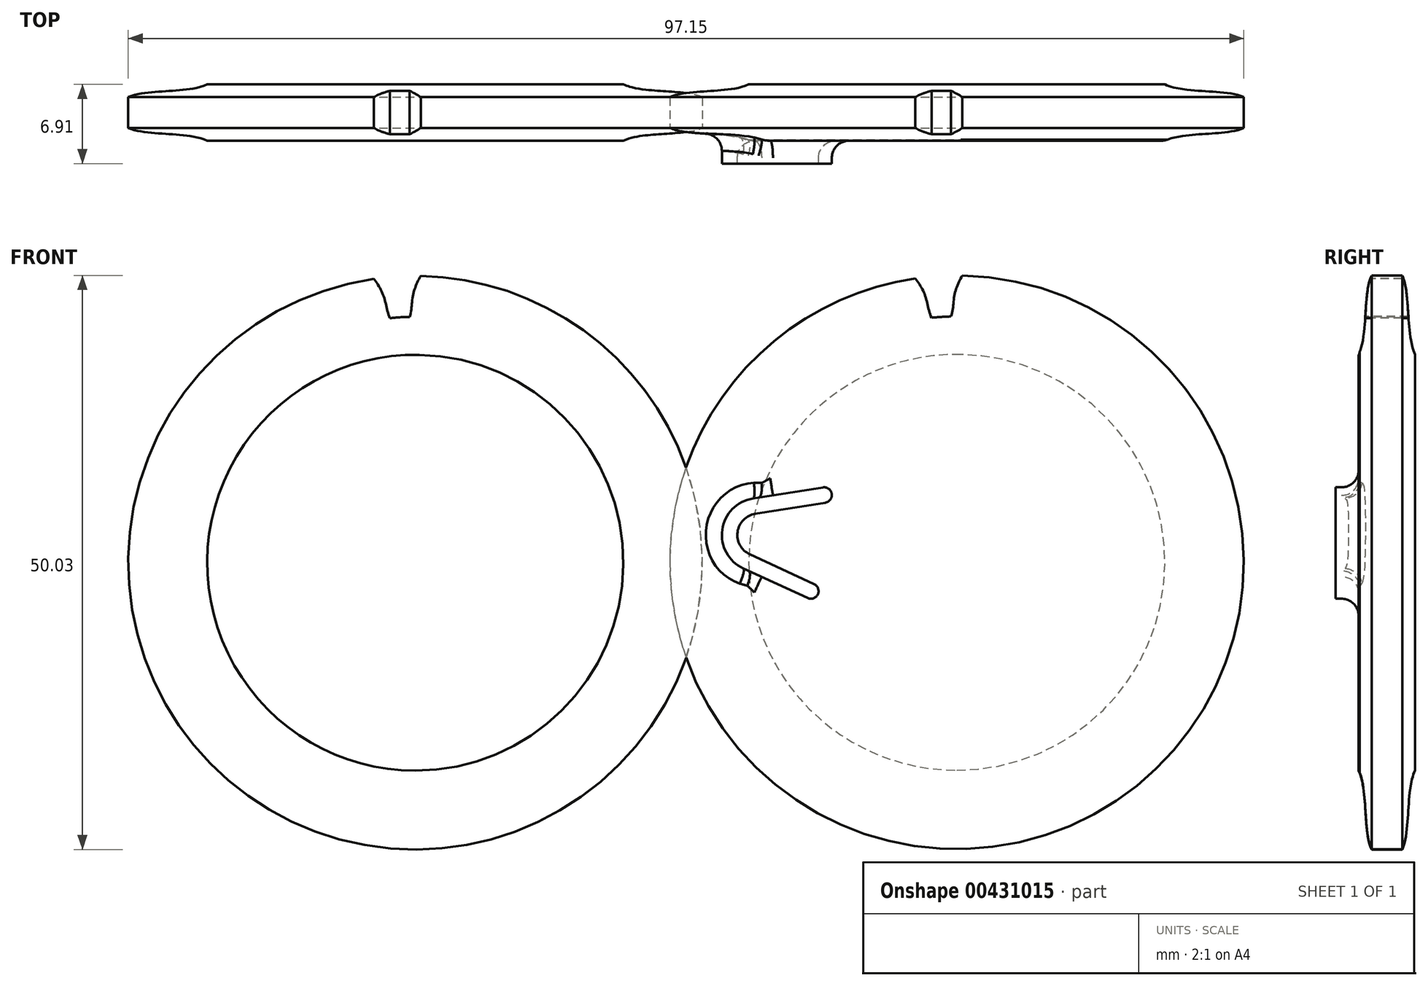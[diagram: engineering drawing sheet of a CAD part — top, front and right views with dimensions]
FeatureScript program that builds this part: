
annotation { "Feature Type Name" : "Feature", "Feature Type Description" : "" }
export const myFeature = defineFeature(function(context is Context, id is Id, definition is map)
    precondition{}
    {
        {
            var Q0;
            Q0=qCreatedBy(makeId("Front.planeOp"),FACE);
            var sketch = newSketch(context, id + "F0", { "sketchPlane" : qUnion([Q0])});
            skCircle(sketch, "E0", {"center": v(0, 0) * mm, "radius": 5.22 * mm});
            skPoint(sketch, "E0.first.point", {"position": v(-0.14, 5.22) * mm});
            skPoint(sketch, "E0.second.point", {"position": v(0.18, -5.22) * mm});
            skPoint(sketch, "E0.third.point", {"position": v(5.22, 0.15) * mm});
            skSolve(sketch);
        }
        {
            var Q0;
            Q0=qCreatedBy(makeId("Front.planeOp"),FACE);
            var sketch = newSketch(context, id + "F1", { "sketchPlane" : qUnion([Q0])});
            skCircle(sketch, "E1.0", {"center": v(0, 0) * mm, "radius": 5.22 * mm});
            skLineSegment(sketch, "E2", {"start": v(0, 125) * mm, "end": v(0, -125) * mm, "construction": true});
            skLineSegment(sketch, "E3", {"start": v(-125, 0) * mm, "end": v(125, 0) * mm, "construction": true});
            skArc(sketch, "E4", {"start": v(-3.61, 24.74) * mm, "mid": v(1.57, -24.95) * mm, "end": v(0.48, 25) * mm, "construction": true});
            skCircle(sketch, "E5", {"center": v(0, 0) * mm, "radius": 23.24 * mm, "construction": true});
            skCircle(sketch, "E6", {"center": v(0, 0) * mm, "radius": 21.43 * mm, "construction": true});
            skLineSegment(sketch, "E7", {"start": v(0, 0) * mm, "end": v(-4.4, 25.96) * mm, "construction": true});
            skLineSegment(sketch, "E8", {"start": v(0, 0) * mm, "end": v(1.13, 26.88) * mm, "construction": true});
            skFitSpline(sketch, "E9", {"points": [v(-3.61, 24.74) * mm, v(-2.7, 23.08) * mm, v(-2.2, 21.32) * mm, v(-1.5, 20.62) * mm], "startDerivative": vector(3.33, -4.08) * mm, "endDerivative": vector(3.08, -2.02) * mm});
            skFitSpline(sketch, "E10.MirrorCS", {"points": [v(0.48, 25) * mm, v(-0.2, 23.23) * mm, v(-0.5, 21.43) * mm, v(-1.1, 20.65) * mm], "startDerivative": vector(-2.8, -4.47) * mm, "endDerivative": vector(-2.8, -2.4) * mm});
            skArc(sketch, "E11", {"start": v(-2.2, 21.32) * mm, "mid": v(-1.35, 21.39) * mm, "end": v(-0.5, 21.43) * mm});
            skArc(sketch, "E12", {"start": v(-4.17, 24.65) * mm, "mid": v(-3.9, 24.7) * mm, "end": v(-3.61, 24.74) * mm});
            skArc(sketch, "E13.trimOffspring", {"start": v(0.48, 25) * mm, "mid": v(0.77, 24.99) * mm, "end": v(1.05, 24.98) * mm});
            skArc(sketch, "E14.1.0", {"start": v(-4.72, 24.55) * mm, "mid": v(-4.45, 24.6) * mm, "end": v(-4.17, 24.65) * mm});
            skArc(sketch, "E14.1.1", {"start": v(-9.2, 23.24) * mm, "mid": v(-8.94, 23.35) * mm, "end": v(-8.68, 23.45) * mm});
            skArc(sketch, "E14.1.2", {"start": v(-6.58, 20.4) * mm, "mid": v(-5.76, 20.64) * mm, "end": v(-4.94, 20.86) * mm});
            skArc(sketch, "E14.2.0", {"start": v(-9.72, 23.03) * mm, "mid": v(-9.46, 23.14) * mm, "end": v(-9.2, 23.24) * mm});
            skArc(sketch, "E14.2.1", {"start": v(-13.84, 20.82) * mm, "mid": v(-13.6, 20.98) * mm, "end": v(-13.36, 21.13) * mm});
            skArc(sketch, "E14.2.2", {"start": v(-10.68, 18.58) * mm, "mid": v(-9.93, 19) * mm, "end": v(-9.16, 19.37) * mm});
            skArc(sketch, "E14.3.0", {"start": v(-14.3, 20.5) * mm, "mid": v(-14.07, 20.67) * mm, "end": v(-13.84, 20.82) * mm});
            skArc(sketch, "E14.3.1", {"start": v(-17.86, 17.5) * mm, "mid": v(-17.66, 17.7) * mm, "end": v(-17.46, 17.89) * mm});
            skArc(sketch, "E14.3.2", {"start": v(-14.3, 15.96) * mm, "mid": v(-13.66, 16.51) * mm, "end": v(-13, 17.04) * mm});
            skArc(sketch, "E14.4.0", {"start": v(-18.25, 17.08) * mm, "mid": v(-18.06, 17.29) * mm, "end": v(-17.86, 17.5) * mm});
            skArc(sketch, "E14.4.1", {"start": v(-21.1, 13.4) * mm, "mid": v(-20.96, 13.63) * mm, "end": v(-20.8, 13.87) * mm});
            skArc(sketch, "E14.4.2", {"start": v(-17.31, 12.63) * mm, "mid": v(-16.8, 13.31) * mm, "end": v(-16.25, 13.97) * mm});
            skArc(sketch, "E14.5.0", {"start": v(-21.4, 12.92) * mm, "mid": v(-21.26, 13.16) * mm, "end": v(-21.1, 13.4) * mm});
            skArc(sketch, "E14.5.1", {"start": v(-23.43, 8.71) * mm, "mid": v(-23.33, 8.98) * mm, "end": v(-23.23, 9.24) * mm});
            skArc(sketch, "E14.5.2", {"start": v(-19.56, 8.76) * mm, "mid": v(-19.2, 9.53) * mm, "end": v(-18.8, 10.29) * mm});
            skArc(sketch, "E14.6.0", {"start": v(-23.62, 8.18) * mm, "mid": v(-23.53, 8.45) * mm, "end": v(-23.43, 8.71) * mm});
            skArc(sketch, "E14.6.1", {"start": v(-24.73, 3.65) * mm, "mid": v(-24.69, 3.93) * mm, "end": v(-24.64, 4.2) * mm});
            skArc(sketch, "E14.6.2", {"start": v(-20.95, 4.5) * mm, "mid": v(-20.76, 5.33) * mm, "end": v(-20.53, 6.15) * mm});
            skArc(sketch, "E14.7.0", {"start": v(-24.8, 3.1) * mm, "mid": v(-24.77, 3.37) * mm, "end": v(-24.73, 3.65) * mm});
            skArc(sketch, "E14.7.1", {"start": v(-24.95, -1.57) * mm, "mid": v(-24.97, -1.29) * mm, "end": v(-24.98, -1) * mm});
            skArc(sketch, "E14.7.2", {"start": v(-21.43, 0.04) * mm, "mid": v(-21.41, 0.9) * mm, "end": v(-21.36, 1.75) * mm});
            skArc(sketch, "E14.8.0", {"start": v(-24.9, -2.13) * mm, "mid": v(-24.93, -1.85) * mm, "end": v(-24.95, -1.57) * mm});
            skArc(sketch, "E14.8.1", {"start": v(-24.08, -6.72) * mm, "mid": v(-24.15, -6.45) * mm, "end": v(-24.22, -6.18) * mm});
            skArc(sketch, "E14.8.2", {"start": v(-20.97, -4.41) * mm, "mid": v(-21.13, -3.57) * mm, "end": v(-21.26, -2.73) * mm});
            skArc(sketch, "E14.9.0", {"start": v(-23.92, -7.26) * mm, "mid": v(-24, -7) * mm, "end": v(-24.08, -6.72) * mm});
            skArc(sketch, "E14.9.1", {"start": v(-22.15, -11.58) * mm, "mid": v(-22.28, -11.33) * mm, "end": v(-22.4, -11.08) * mm});
            skArc(sketch, "E14.9.2", {"start": v(-19.6, -8.68) * mm, "mid": v(-19.93, -7.9) * mm, "end": v(-20.23, -7.09) * mm});
            skArc(sketch, "E14.10.0", {"start": v(-21.89, -12.08) * mm, "mid": v(-22.02, -11.83) * mm, "end": v(-22.15, -11.58) * mm});
            skArc(sketch, "E14.10.1", {"start": v(-19.26, -15.94) * mm, "mid": v(-19.44, -15.72) * mm, "end": v(-19.62, -15.5) * mm});
            skArc(sketch, "E14.10.2", {"start": v(-17.36, -12.56) * mm, "mid": v(-17.85, -11.86) * mm, "end": v(-18.3, -11.14) * mm});
            skArc(sketch, "E14.11.0", {"start": v(-18.9, -16.37) * mm, "mid": v(-19.08, -16.15) * mm, "end": v(-19.26, -15.94) * mm});
            skArc(sketch, "E14.11.1", {"start": v(-15.53, -19.6) * mm, "mid": v(-15.75, -19.42) * mm, "end": v(-15.97, -19.24) * mm});
            skArc(sketch, "E14.11.2", {"start": v(-14.37, -15.9) * mm, "mid": v(-15, -15.31) * mm, "end": v(-15.6, -14.7) * mm});
            skArc(sketch, "E14.12.0", {"start": v(-15.08, -19.94) * mm, "mid": v(-15.3, -19.77) * mm, "end": v(-15.53, -19.6) * mm});
            skArc(sketch, "E14.12.1", {"start": v(-11.12, -22.4) * mm, "mid": v(-11.37, -22.27) * mm, "end": v(-11.62, -22.14) * mm});
            skArc(sketch, "E14.12.2", {"start": v(-10.75, -18.54) * mm, "mid": v(-11.48, -18.1) * mm, "end": v(-12.2, -17.62) * mm});
            skArc(sketch, "E14.13.0", {"start": v(-10.6, -22.64) * mm, "mid": v(-10.86, -22.52) * mm, "end": v(-11.12, -22.4) * mm});
            skArc(sketch, "E14.13.1", {"start": v(-6.22, -24.21) * mm, "mid": v(-6.49, -24.14) * mm, "end": v(-6.76, -24.07) * mm});
            skArc(sketch, "E14.13.2", {"start": v(-6.66, -20.37) * mm, "mid": v(-7.47, -20.09) * mm, "end": v(-8.26, -19.77) * mm});
            skArc(sketch, "E14.14.0", {"start": v(-5.67, -24.35) * mm, "mid": v(-5.94, -24.28) * mm, "end": v(-6.22, -24.21) * mm});
            skArc(sketch, "E14.14.1", {"start": v(-1.05, -24.98) * mm, "mid": v(-1.33, -24.96) * mm, "end": v(-1.6, -24.95) * mm});
            skArc(sketch, "E14.14.2", {"start": v(-2.28, -21.3) * mm, "mid": v(-3.13, -21.2) * mm, "end": v(-3.97, -21.06) * mm});
            skArc(sketch, "E14.15.0", {"start": v(-0.48, -25) * mm, "mid": v(-0.77, -24.99) * mm, "end": v(-1.05, -24.98) * mm});
            skArc(sketch, "E14.15.1", {"start": v(4.17, -24.65) * mm, "mid": v(3.9, -24.7) * mm, "end": v(3.61, -24.74) * mm});
            skArc(sketch, "E14.15.2", {"start": v(2.2, -21.32) * mm, "mid": v(1.35, -21.39) * mm, "end": v(0.5, -21.43) * mm});
            skArc(sketch, "E14.16.0", {"start": v(4.72, -24.55) * mm, "mid": v(4.45, -24.6) * mm, "end": v(4.17, -24.65) * mm});
            skArc(sketch, "E14.16.1", {"start": v(9.2, -23.24) * mm, "mid": v(8.94, -23.35) * mm, "end": v(8.68, -23.45) * mm});
            skArc(sketch, "E14.16.2", {"start": v(6.58, -20.4) * mm, "mid": v(5.76, -20.64) * mm, "end": v(4.94, -20.86) * mm});
            skArc(sketch, "E14.17.0", {"start": v(9.72, -23.03) * mm, "mid": v(9.46, -23.14) * mm, "end": v(9.2, -23.24) * mm});
            skArc(sketch, "E14.17.1", {"start": v(13.84, -20.82) * mm, "mid": v(13.6, -20.98) * mm, "end": v(13.36, -21.13) * mm});
            skArc(sketch, "E14.17.2", {"start": v(10.68, -18.58) * mm, "mid": v(9.93, -19) * mm, "end": v(9.16, -19.37) * mm});
            skArc(sketch, "E14.18.0", {"start": v(14.3, -20.5) * mm, "mid": v(14.07, -20.67) * mm, "end": v(13.84, -20.82) * mm});
            skArc(sketch, "E14.18.1", {"start": v(17.86, -17.5) * mm, "mid": v(17.66, -17.7) * mm, "end": v(17.46, -17.89) * mm});
            skArc(sketch, "E14.18.2", {"start": v(14.3, -15.96) * mm, "mid": v(13.66, -16.51) * mm, "end": v(13, -17.04) * mm});
            skArc(sketch, "E14.19.0", {"start": v(18.25, -17.08) * mm, "mid": v(18.06, -17.29) * mm, "end": v(17.86, -17.5) * mm});
            skArc(sketch, "E14.19.1", {"start": v(21.1, -13.4) * mm, "mid": v(20.96, -13.63) * mm, "end": v(20.8, -13.87) * mm});
            skArc(sketch, "E14.19.2", {"start": v(17.31, -12.63) * mm, "mid": v(16.8, -13.31) * mm, "end": v(16.25, -13.97) * mm});
            skArc(sketch, "E14.20.0", {"start": v(21.4, -12.92) * mm, "mid": v(21.26, -13.16) * mm, "end": v(21.1, -13.4) * mm});
            skArc(sketch, "E14.20.1", {"start": v(23.43, -8.71) * mm, "mid": v(23.33, -8.98) * mm, "end": v(23.23, -9.24) * mm});
            skArc(sketch, "E14.20.2", {"start": v(19.56, -8.76) * mm, "mid": v(19.2, -9.53) * mm, "end": v(18.8, -10.29) * mm});
            skArc(sketch, "E14.21.0", {"start": v(23.62, -8.18) * mm, "mid": v(23.53, -8.45) * mm, "end": v(23.43, -8.71) * mm});
            skArc(sketch, "E14.21.1", {"start": v(24.73, -3.65) * mm, "mid": v(24.69, -3.93) * mm, "end": v(24.64, -4.2) * mm});
            skArc(sketch, "E14.21.2", {"start": v(20.95, -4.5) * mm, "mid": v(20.76, -5.33) * mm, "end": v(20.53, -6.15) * mm});
            skArc(sketch, "E14.22.0", {"start": v(24.8, -3.1) * mm, "mid": v(24.77, -3.37) * mm, "end": v(24.73, -3.65) * mm});
            skArc(sketch, "E14.22.1", {"start": v(24.95, 1.57) * mm, "mid": v(24.97, 1.29) * mm, "end": v(24.98, 1) * mm});
            skArc(sketch, "E14.22.2", {"start": v(21.43, -0.04) * mm, "mid": v(21.41, -0.9) * mm, "end": v(21.36, -1.75) * mm});
            skArc(sketch, "E14.23.0", {"start": v(24.9, 2.13) * mm, "mid": v(24.93, 1.85) * mm, "end": v(24.95, 1.57) * mm});
            skArc(sketch, "E14.23.1", {"start": v(24.08, 6.72) * mm, "mid": v(24.15, 6.45) * mm, "end": v(24.22, 6.18) * mm});
            skArc(sketch, "E14.23.2", {"start": v(20.97, 4.41) * mm, "mid": v(21.13, 3.57) * mm, "end": v(21.26, 2.73) * mm});
            skArc(sketch, "E14.24.0", {"start": v(23.92, 7.26) * mm, "mid": v(24, 7) * mm, "end": v(24.08, 6.72) * mm});
            skArc(sketch, "E14.24.1", {"start": v(22.15, 11.58) * mm, "mid": v(22.28, 11.33) * mm, "end": v(22.4, 11.08) * mm});
            skArc(sketch, "E14.24.2", {"start": v(19.6, 8.68) * mm, "mid": v(19.93, 7.9) * mm, "end": v(20.23, 7.09) * mm});
            skArc(sketch, "E14.25.0", {"start": v(21.89, 12.08) * mm, "mid": v(22.02, 11.83) * mm, "end": v(22.15, 11.58) * mm});
            skArc(sketch, "E14.25.1", {"start": v(19.26, 15.94) * mm, "mid": v(19.44, 15.72) * mm, "end": v(19.62, 15.5) * mm});
            skArc(sketch, "E14.25.2", {"start": v(17.36, 12.56) * mm, "mid": v(17.85, 11.86) * mm, "end": v(18.3, 11.14) * mm});
            skArc(sketch, "E14.26.0", {"start": v(18.9, 16.37) * mm, "mid": v(19.08, 16.15) * mm, "end": v(19.26, 15.94) * mm});
            skArc(sketch, "E14.26.1", {"start": v(15.53, 19.6) * mm, "mid": v(15.75, 19.42) * mm, "end": v(15.97, 19.24) * mm});
            skArc(sketch, "E14.26.2", {"start": v(14.37, 15.9) * mm, "mid": v(15, 15.31) * mm, "end": v(15.6, 14.7) * mm});
            skArc(sketch, "E14.27.0", {"start": v(15.08, 19.94) * mm, "mid": v(15.3, 19.77) * mm, "end": v(15.53, 19.6) * mm});
            skArc(sketch, "E14.27.1", {"start": v(11.12, 22.4) * mm, "mid": v(11.37, 22.27) * mm, "end": v(11.62, 22.14) * mm});
            skArc(sketch, "E14.27.2", {"start": v(10.75, 18.54) * mm, "mid": v(11.48, 18.1) * mm, "end": v(12.2, 17.62) * mm});
            skArc(sketch, "E14.28.0", {"start": v(10.6, 22.64) * mm, "mid": v(10.86, 22.52) * mm, "end": v(11.12, 22.4) * mm});
            skArc(sketch, "E14.28.1", {"start": v(6.22, 24.21) * mm, "mid": v(6.49, 24.14) * mm, "end": v(6.76, 24.07) * mm});
            skArc(sketch, "E14.28.2", {"start": v(6.66, 20.37) * mm, "mid": v(7.47, 20.09) * mm, "end": v(8.26, 19.77) * mm});
            skArc(sketch, "E14.29.0", {"start": v(5.67, 24.35) * mm, "mid": v(5.94, 24.28) * mm, "end": v(6.22, 24.21) * mm});
            skArc(sketch, "E14.29.1", {"start": v(1.05, 24.98) * mm, "mid": v(1.33, 24.96) * mm, "end": v(1.6, 24.95) * mm});
            skArc(sketch, "E14.29.2", {"start": v(2.28, 21.3) * mm, "mid": v(3.13, 21.2) * mm, "end": v(3.97, 21.06) * mm});
            skArc(sketch, "E15", {"start": v(-3.61, 24.74) * mm, "mid": v(-1.57, 24.95) * mm, "end": v(0.48, 25) * mm});
            skCircle(sketch, "E16", {"center": v(-47.16, -0.04) * mm, "radius": 21.4 * mm});
            skPoint(sketch, "E16.first.point", {"position": v(-56.55, 19.18) * mm});
            skPoint(sketch, "E16.second.point", {"position": v(-28.26, -10.06) * mm});
            skPoint(sketch, "E16.third.point", {"position": v(-59.13, -17.76) * mm});
            skSolve(sketch);
        }
        {
            var Q0;
            Q0=qCreatedBy(makeId("Right.planeOp"),FACE);
            var sketch = newSketch(context, id + "F2", { "sketchPlane" : qUnion([Q0])});
            skPoint(sketch, "E17.0", {"position": v(0, 26.88) * mm});
            skLineSegment(sketch, "E18.bottom", {"start": v(4.9, 0) * mm, "end": v(0, 0) * mm});
            skLineSegment(sketch, "E18.top", {"start": v(3.79, 25) * mm, "end": v(1.12, 25) * mm});
            skLineSegment(sketch, "E18.left", {"start": v(0, 5.22) * mm, "end": v(0, 9.34) * mm});
            skPoint(sketch, "E19.0", {"position": v(0, 5.22) * mm});
            skLineSegment(sketch, "E20.bottom", {"start": v(0, 0) * mm, "end": v(4.9, 0) * mm});
            skLineSegment(sketch, "E21", {"start": v(2.45, 26.88) * mm, "end": v(2.45, -4.73) * mm, "construction": true});
            skFitSpline(sketch, "E22", {"points": [v(1.12, 25) * mm, v(0, 18.12) * mm], "startDerivative": vector(-2.23, -4.75) * mm, "endDerivative": vector(-2.47, -5.27) * mm});
            skLineSegment(sketch, "E23.right", {"start": v(0, 18.12) * mm, "end": v(0, 9.34) * mm});
            skFitSpline(sketch, "E24.MirrorCS", {"points": [v(3.79, 25) * mm, v(4.9, 18.12) * mm], "startDerivative": vector(2.23, -4.75) * mm, "endDerivative": vector(2.47, -5.27) * mm});
            skLineSegment(sketch, "E25.MirrorCS", {"start": v(4.9, 18.12) * mm, "end": v(4.9, 18.12) * mm});
            skLineSegment(sketch, "E26.MirrorCS", {"start": v(4.9, 18.12) * mm, "end": v(4.9, 9.34) * mm});
            skLineSegment(sketch, "E27.MirrorCS", {"start": v(4.9, 9.34) * mm, "end": v(4.9, 9.71) * mm});
            skPoint(sketch, "E28.orphan", {"position": v(4.9, 26.88) * mm});
            skPoint(sketch, "E29.visualSharp", {"position": v(0, 9.34) * mm});
            skPoint(sketch, "E30.visualSharp", {"position": v(4.9, 9.34) * mm});
            skLineSegment(sketch, "E30.filletArc", {"start": v(4.9, 9.71) * mm, "end": v(4.9, 9.71) * mm});
            skPoint(sketch, "E31.0", {"position": v(0, 25.96) * mm});
            skLineSegment(sketch, "E32", {"start": v(0, 25) * mm, "end": v(13.28, 25) * mm, "construction": true});
            skLineSegment(sketch, "E33.0", {"start": v(0, -25) * mm, "end": v(0, 0) * mm, "construction": true});
            skLineSegment(sketch, "E34.bottom", {"start": v(0, 5.22) * mm, "end": v(0, 5.22) * mm});
            skLineSegment(sketch, "E34.right", {"start": v(0, 5.22) * mm, "end": v(0, 0) * mm});
            skLineSegment(sketch, "E35.trimOffspring", {"start": v(0, 5.22) * mm, "end": v(0, 25) * mm, "construction": true});
            skLineSegment(sketch, "E36", {"start": v(4.9, 9.34) * mm, "end": v(4.9, 5.22) * mm});
            skLineSegment(sketch, "E37", {"start": v(4.9, 5.22) * mm, "end": v(4.9, 0) * mm});
            skSolve(sketch);
        }
        {
            var Q0;
            Q0=makeQuery(id+"F2.imprint","IMPRINT",FACE,{"disambiguationData":[TD([[makeQuery(id+"F2.imprint","IMPRINT",EDGE,{"derivedFrom":sQuery(id+"F2.wireOp",EDGE,"E18.top")}),1.0]])]});
            var Q1;
            {var subQ5=sQuery(id+"F2.wireOp",EDGE,"E20.left");Q1=makeQuery(id+"F2.imprint","IMPRINT",FACE,{"disambiguationData":[TD([[makeQuery(id+"F2.imprint","IMPRINT",EDGE,{"derivedFrom":subQ5}),-1.0]])]});}
            var Q2;
            {var subQ0=sQuery(id+"F2.wireOp",EDGE,"E20.right");Q2=makeQuery(id+"F2.imprint","IMPRINT",FACE,{"disambiguationData":[TD([[makeQuery(id+"F2.imprint","IMPRINT",EDGE,{"derivedFrom":subQ0}),1.0]])]});}
            var Q3;
            Q3=sQuery(id+"F2.wireOp",EDGE,"E20.bottom");
            revolve(context, id + "F3", {"entities" : qUnion([Q0, Q1, Q2]), "axis" : qUnion([Q3]), "revolveType" : RevolveType.FULL});
        }
        {
            var Q0;
            Q0=makeQuery(id+"F1.imprint","IMPRINT",FACE,{"disambiguationData":[TD([[makeQuery(id+"F1.imprint","IMPRINT",EDGE,{"derivedFrom":sQuery(id+"F1.wireOp",EDGE,"E9")}),1.0]])]});
            extrude(context, id + "F4", {"entities" : qUnion([Q0]), "operationType" : NewBodyOperationType.REMOVE, "endBound" : BoundingType.THROUGH_ALL, "oppositeDirection" : true, "depth" : 25 * mm});
        }
        {
            var Q0;
            Q0=makeQuery(id+"F3.opRevolve","SWEPT_BODY",BODY,{"disambiguationData":[OSD([sQuery(id+"F2.wireOp",EDGE,"E18.top"),sQuery(id+"F2.wireOp",EDGE,"E18.left"),sQuery(id+"F2.wireOp",EDGE,"E20.bottom"),sQuery(id+"F2.wireOp",EDGE,"E22"),sQuery(id+"F2.wireOp",EDGE,"E23.right"),sQuery(id+"F2.wireOp",EDGE,"E24.MirrorCS"),sQuery(id+"F2.wireOp",EDGE,"E26.MirrorCS"),sQuery(id+"F2.wireOp",EDGE,"E27.MirrorCS"),sQuery(id+"F2.wireOp",EDGE,"E34.right"),sQuery(id+"F2.wireOp",EDGE,"E36"),sQuery(id+"F2.wireOp",EDGE,"E37")])]});
            var Q1;
            Q1=sQuery(id+"F1.wireOp",VERTEX,"E1.0.center");
            var Q2;
            Q2=sQuery(id+"F1.wireOp",VERTEX,"E16.center");
            transform(context, id + "F5", {"entities" : qUnion([Q0]), "transformType" : TransformType.TRANSLATION_ENTITY, "oppositeDirectionEntity" : false, "transformLine" : qUnion([Q1, Q2]), "makeCopy" : true});
        }
        {
            var Q0;
            Q0=makeQuery(id+"F3.opRevolve","SWEPT_FACE",FACE,{"disambiguationData":[OSD([sQuery(id+"F2.wireOp",EDGE,"E23.right")])]});
            var sketch = newSketch(context, id + "F6", { "sketchPlane" : qUnion([Q0])});
            skLineSegment(sketch, "E38", {"start": v(-11.66, 6.53) * mm, "end": v(-17.76, 5.56) * mm});
            skLineSegment(sketch, "E39", {"start": v(-13, -3.11) * mm, "end": v(-18.6, -0.52) * mm});
            skArc(sketch, "E40", {"start": v(-17.76, 5.56) * mm, "mid": v(-20.43, 2.83) * mm, "end": v(-18.6, -0.52) * mm});
            skLineSegment(sketch, "E41.0", {"start": v(-12.43, -1.89) * mm, "end": v(-18.03, 0.7) * mm});
            skArc(sketch, "E41.1", {"start": v(-17.54, 4.23) * mm, "mid": v(-19.1, 2.64) * mm, "end": v(-18.03, 0.7) * mm});
            skLineSegment(sketch, "E41.2", {"start": v(-11.45, 5.2) * mm, "end": v(-17.54, 4.23) * mm});
            skCircle(sketch, "E42.0", {"center": v(0, 0) * mm, "radius": 23.12 * mm});
            skArc(sketch, "E43", {"start": v(-11.45, 5.2) * mm, "mid": v(-10.9, 5.97) * mm, "end": v(-11.66, 6.53) * mm});
            skLineSegment(sketch, "E44", {"start": v(-17.25, 2.39) * mm, "end": v(-16.66, 2.39) * mm, "construction": true});
            skLineSegment(sketch, "E45", {"start": v(0, 0) * mm, "end": v(-17.25, 2.39) * mm, "construction": true});
            skArc(sketch, "E46.MirrorCS", {"start": v(-12.43, -1.89) * mm, "mid": v(-12.1, -2.79) * mm, "end": v(-13, -3.11) * mm});
            skArc(sketch, "E47.0", {"start": v(-18.1, -0.75) * mm, "mid": v(17.95, -2.49) * mm, "end": v(-17.22, 5.64) * mm});
            skArc(sketch, "E48.trimOffspring", {"start": v(-17.63, 4.2) * mm, "mid": v(-17.95, 2.49) * mm, "end": v(-18.1, 0.74) * mm});
            skSolve(sketch);
        }
        {
            var Q0;
            {var subQ5=sQuery(id+"F6.wireOp",EDGE,"E40");Q0=makeQuery(id+"F6.imprint","IMPRINT",FACE,{"disambiguationData":[TD([[makeQuery(id+"F6.imprint","IMPRINT",EDGE,{"derivedFrom":subQ5}),1.0]])]});}
            var Q1;
            {var subQ1=sQuery(id+"F6.wireOp",EDGE,"E41.0");Q1=makeQuery(id+"F6.imprint","IMPRINT",FACE,{"disambiguationData":[TD([[makeQuery(id+"F6.imprint","IMPRINT",EDGE,{"derivedFrom":subQ1}),1.0]])]});}
            var Q2;
            {var subQ0=sQuery(id+"F6.wireOp",EDGE,"E41.2");Q2=makeQuery(id+"F6.imprint","IMPRINT",FACE,{"disambiguationData":[TD([[makeQuery(id+"F6.imprint","IMPRINT",EDGE,{"derivedFrom":subQ0}),-1.0]])]});}
            extrude(context, id + "F7", {"entities" : qUnion([Q0, Q1, Q2]), "depth" : 2 * mm, "hasSecondDirection" : true, "secondDirectionOppositeDirection" : true, "secondDirectionDepth" : 2 * mm});
        }
        {
            var Q0;
            Q0=makeQuery(id+"F3.opRevolve","SWEPT_BODY",BODY,{"disambiguationData":[OSD([sQuery(id+"F2.wireOp",EDGE,"E18.top"),sQuery(id+"F2.wireOp",EDGE,"E18.left"),sQuery(id+"F2.wireOp",EDGE,"E20.bottom"),sQuery(id+"F2.wireOp",EDGE,"E20.top"),sQuery(id+"F2.wireOp",EDGE,"E20.right"),sQuery(id+"F2.wireOp",EDGE,"E22"),sQuery(id+"F2.wireOp",EDGE,"E23.right"),sQuery(id+"F2.wireOp",EDGE,"E24.MirrorCS"),sQuery(id+"F2.wireOp",EDGE,"E26.MirrorCS"),sQuery(id+"F2.wireOp",EDGE,"E27.MirrorCS"),sQuery(id+"F2.wireOp",EDGE,"wCEg8Sva-JeQy-TYcz-iyIM-gMDkAqgUJc6i.top"),sQuery(id+"F2.wireOp",EDGE,"wCEg8Sva-JeQy-TYcz-iyIM-gMDkAqgUJc6i.right"),sQuery(id+"F2.wireOp",EDGE,"51bb832b-4c8d-4cbf-9256-66539f511a6b.filletArc"),sQuery(id+"F2.wireOp",EDGE,"07d73420-b508-4266-b820-63697a5285c9.filletArc"),sQuery(id+"F2.wireOp",EDGE,"E34.right"),sQuery(id+"F2.wireOp",EDGE,"E36")])]});
            var Q1;
            Q1=makeQuery(id+"F7.opExtrude","SWEPT_BODY",BODY,{"disambiguationData":[OSD([sQuery(id+"F6.wireOp",EDGE,"E38"),sQuery(id+"F6.wireOp",EDGE,"E39"),sQuery(id+"F6.wireOp",EDGE,"E40"),sQuery(id+"F6.wireOp",EDGE,"E41.0"),sQuery(id+"F6.wireOp",EDGE,"E41.1"),sQuery(id+"F6.wireOp",EDGE,"E41.2"),sQuery(id+"F6.wireOp",EDGE,"E43"),sQuery(id+"F6.wireOp",EDGE,"E46.MirrorCS")])]});
            booleanBodies(context, id + "F8", {"operationType" : BooleanOperationType.UNION, "tools" : qUnion([Q0, Q1])});
        }
        {
            var Q0;
            Q0=makeQuery(id+"F8.opBoolean","INTERSECT",EDGE,{"derivedFrom":[makeQuery(id+"F3.opRevolve","SWEPT_FACE",FACE,{"disambiguationData":[OSD([sQuery(id+"F2.wireOp",EDGE,"E22")])]}),makeQuery(id+"F7.opExtrude","SWEPT_FACE",FACE,{"disambiguationData":[OSD([sQuery(id+"F6.wireOp",EDGE,"E40")])]})]});
            var Q1;
            Q1=makeQuery(id+"F8.opBoolean","INTERSECT",EDGE,{"derivedFrom":[makeQuery(id+"F3.opRevolve","SWEPT_FACE",FACE,{"disambiguationData":[OSD([sQuery(id+"F2.wireOp",EDGE,"E18.left"),sQuery(id+"F2.wireOp",EDGE,"E23.right"),sQuery(id+"F2.wireOp",EDGE,"E34.right")])]}),makeQuery(id+"F7.opExtrude","SWEPT_FACE",FACE,{"disambiguationData":[OSD([sQuery(id+"F6.wireOp",EDGE,"E39")])]})]});
            var Q2;
            Q2=makeQuery(id+"F8.opBoolean","INTERSECT",EDGE,{"derivedFrom":[makeQuery(id+"F3.opRevolve","SWEPT_FACE",FACE,{"disambiguationData":[OSD([sQuery(id+"F2.wireOp",EDGE,"E22")])]}),makeQuery(id+"F7.opExtrude","SWEPT_FACE",FACE,{"disambiguationData":[OSD([sQuery(id+"F6.wireOp",EDGE,"E41.1")])]})]});
            var Q3;
            Q3=makeQuery(id+"F8.opBoolean","INTERSECT",EDGE,{"derivedFrom":[makeQuery(id+"F3.opRevolve","SWEPT_FACE",FACE,{"disambiguationData":[OSD([sQuery(id+"F2.wireOp",EDGE,"E18.left"),sQuery(id+"F2.wireOp",EDGE,"E23.right"),sQuery(id+"F2.wireOp",EDGE,"E34.right")])]}),makeQuery(id+"F7.opExtrude","SWEPT_FACE",FACE,{"disambiguationData":[OSD([sQuery(id+"F6.wireOp",EDGE,"E38")])]})]});
            var Q4;
            Q4=makeQuery(id+"F3.opRevolve","SWEPT_FACE",FACE,{"disambiguationData":[OSD([sQuery(id+"F2.wireOp",EDGE,"E18.left"),sQuery(id+"F2.wireOp",EDGE,"E23.right"),sQuery(id+"F2.wireOp",EDGE,"E34.right")])]});
            fillet(context, id + "F9", {"entities" : qUnion([Q0, Q1, Q2, Q3, Q4]), "radius" : 1.5 * mm, "tangentPropagation" : true, "allowEdgeOverflow" : false});
        }
    });
